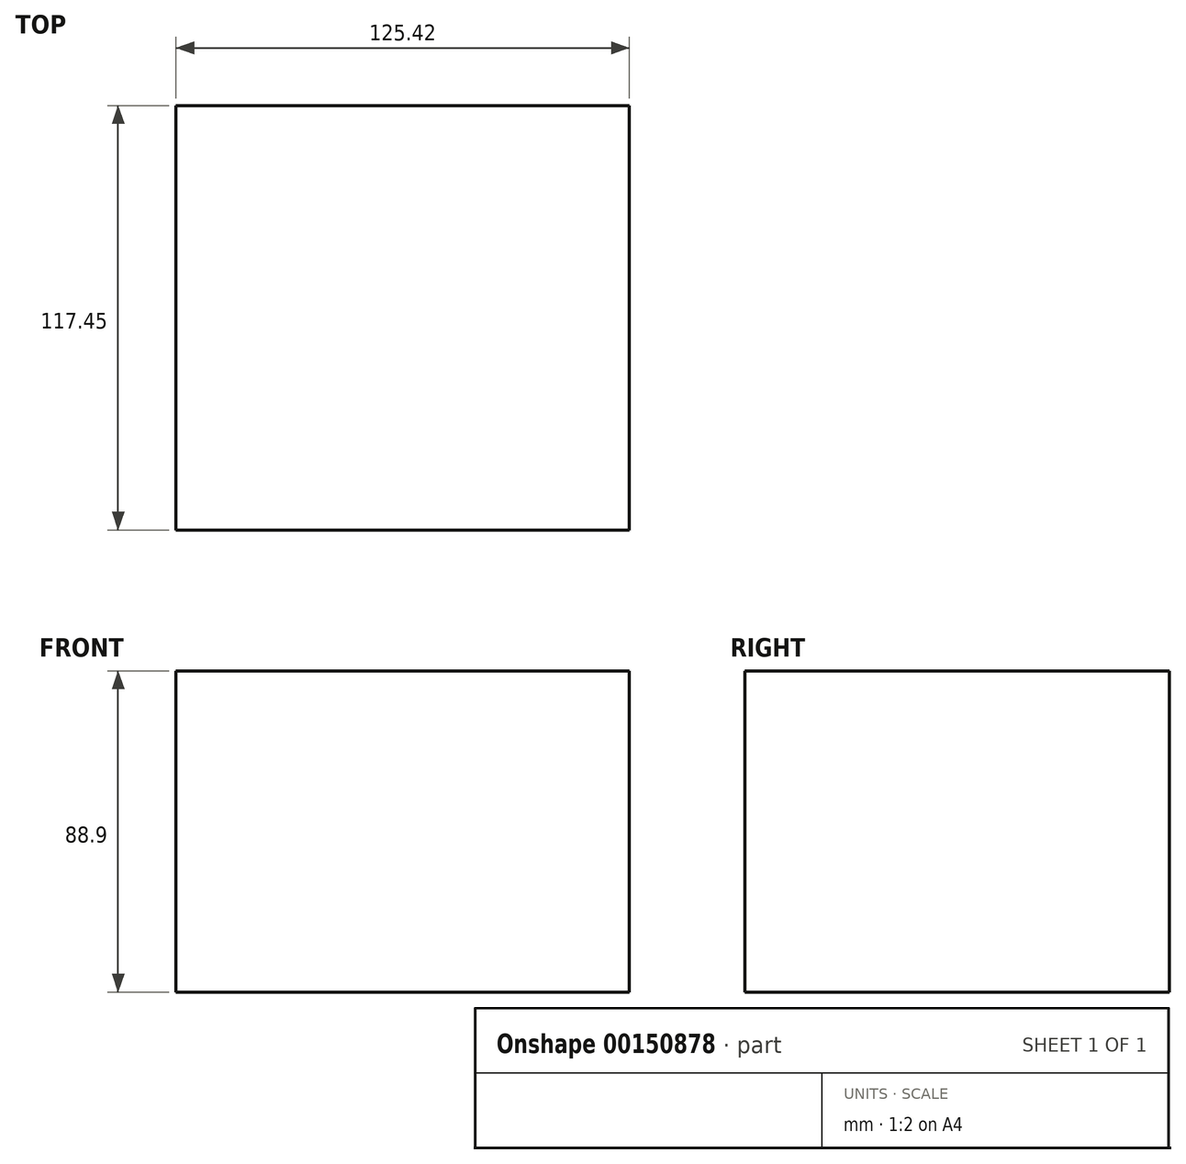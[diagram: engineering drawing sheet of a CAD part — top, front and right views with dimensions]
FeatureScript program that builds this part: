
annotation { "Feature Type Name" : "Feature", "Feature Type Description" : "" }
export const myFeature = defineFeature(function(context is Context, id is Id, definition is map)
    precondition{}
    {
        {
            var Q0;
            Q0=qCreatedBy(makeId("Top.planeOp"),FACE);
            var sketch = newSketch(context, id + "F0", { "sketchPlane" : qUnion([Q0])});
            skLineSegment(sketch, "E0.bottom", {"start": v(-62.38, 93.24) * mm, "end": v(63.04, 93.24) * mm});
            skLineSegment(sketch, "E0.top", {"start": v(-62.38, -24.21) * mm, "end": v(63.04, -24.21) * mm});
            skLineSegment(sketch, "E0.left", {"start": v(-62.38, 93.24) * mm, "end": v(-62.38, -24.21) * mm});
            skLineSegment(sketch, "E0.right", {"start": v(63.04, 93.24) * mm, "end": v(63.04, -24.21) * mm});
            skSolve(sketch);
        }
        {
            var Q0;
            Q0 = qSketchRegion(id + "F0", true);
            extrude(context, id + "F1", {"entities" : qUnion([Q0]), "depth" : 88.9 * mm});
        }
    });
